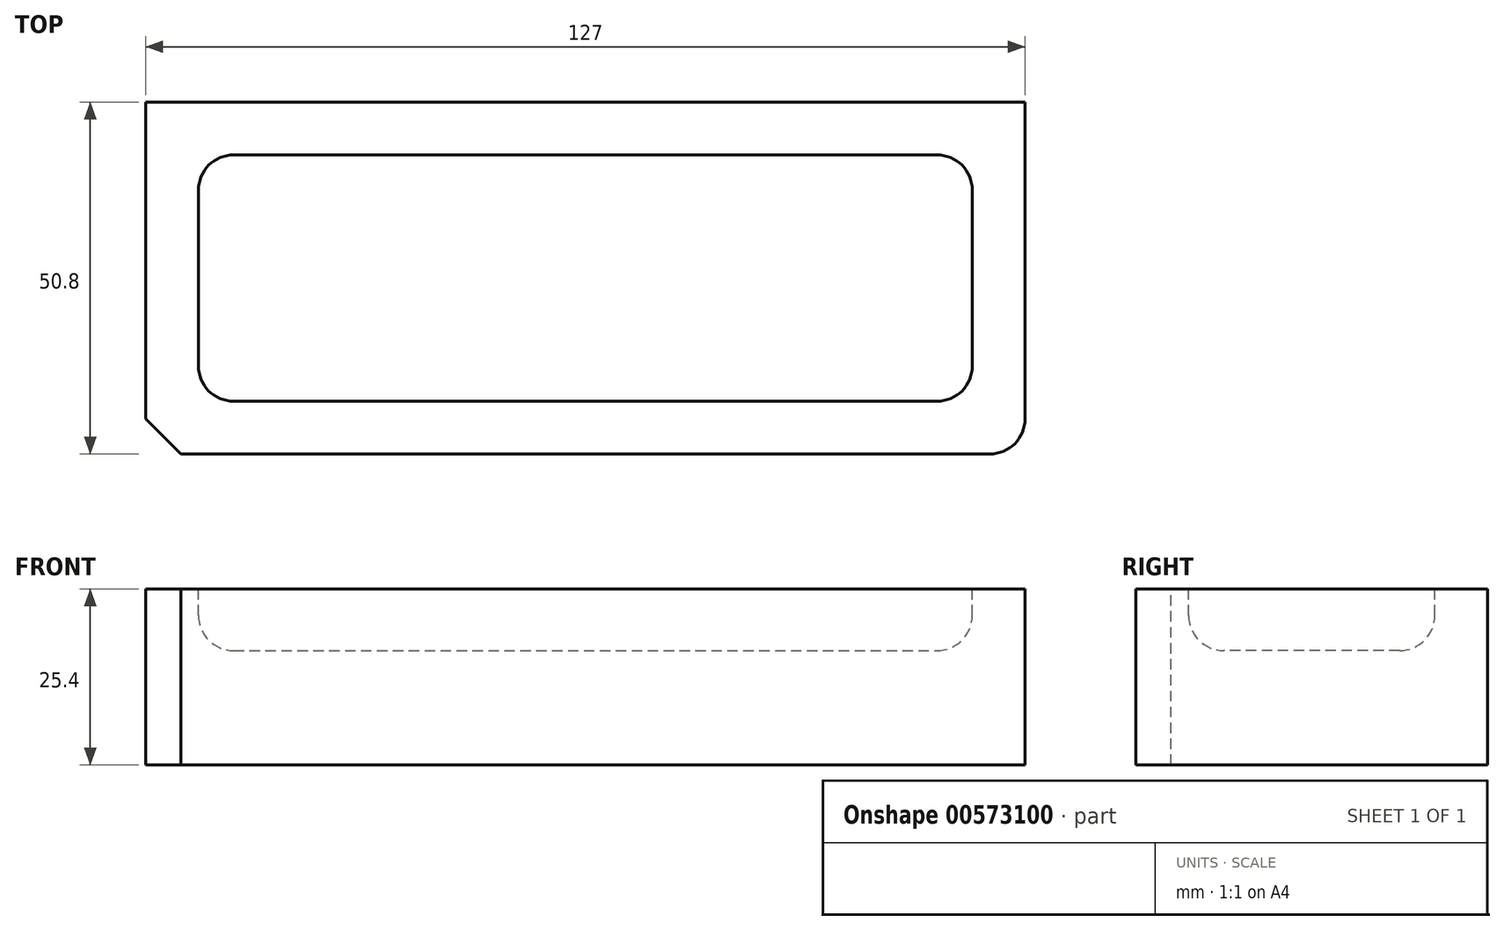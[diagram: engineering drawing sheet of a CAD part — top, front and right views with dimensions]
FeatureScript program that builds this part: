
annotation { "Feature Type Name" : "Feature", "Feature Type Description" : "" }
export const myFeature = defineFeature(function(context is Context, id is Id, definition is map)
    precondition{}
    {
        {
            var Q0;
            Q0=qCreatedBy(makeId("Top.planeOp"),FACE);
            var sketch = newSketch(context, id + "F0", { "sketchPlane" : qUnion([Q0])});
            skLineSegment(sketch, "E0.bottom", {"start": v(-63.5, 25.4) * mm, "end": v(63.5, 25.4) * mm});
            skLineSegment(sketch, "E0.top", {"start": v(-63.5, -25.4) * mm, "end": v(63.5, -25.4) * mm});
            skLineSegment(sketch, "E0.left", {"start": v(-63.5, 25.4) * mm, "end": v(-63.5, -25.4) * mm});
            skLineSegment(sketch, "E0.right", {"start": v(63.5, 25.4) * mm, "end": v(63.5, -25.4) * mm});
            skPoint(sketch, "E0.middle", {"position": v(0, 0) * mm});
            skSolve(sketch);
        }
        {
            var Q0;
            Q0=makeQuery(id+"F0.imprint","IMPRINT",FACE,{"disambiguationData":[TD([[makeQuery(id+"F0.imprint","IMPRINT",EDGE,{"derivedFrom":sQuery(id+"F0.wireOp",EDGE,"E0.bottom")}),-1.0]])]});
            extrude(context, id + "F1", {"entities" : qUnion([Q0]), "depth" : 25.4 * mm, "offsetDistance" : 25.4 * mm});
        }
        {
            var Q0;
            Q0=makeQuery(id+"F1.opExtrude","SWEPT_EDGE",EDGE,{"disambiguationData":[OSD([sQuery(id+"F0.wireOp",EDGE,"E0.top"),sQuery(id+"F0.wireOp",EDGE,"E0.left")])]});
            chamfer(context, id + "F2", {"entities" : qUnion([Q0]), "width" : 5.08 * mm, "tangentPropagation" : true});
        }
        {
            var Q0;
            Q0=makeQuery(id+"F1.opExtrude","SWEPT_EDGE",EDGE,{"disambiguationData":[OSD([sQuery(id+"F0.wireOp",EDGE,"E0.top"),sQuery(id+"F0.wireOp",EDGE,"E0.right")])]});
            fillet(context, id + "F3", {"entities" : qUnion([Q0]), "radius" : 5.08 * mm, "tangentPropagation" : true, "allowEdgeOverflow" : false});
        }
        {
            var Q0;
            Q0=makeQuery(id+"F1.opExtrude","CAP_FACE",FACE,{"disambiguationData":[OSD([sQuery(id+"F0.wireOp",EDGE,"E0.bottom"),sQuery(id+"F0.wireOp",EDGE,"E0.top"),sQuery(id+"F0.wireOp",EDGE,"E0.left"),sQuery(id+"F0.wireOp",EDGE,"E0.right")])],"isStart":false});
            var sketch = newSketch(context, id + "F4", { "sketchPlane" : qUnion([Q0])});
            skLineSegment(sketch, "E1.0", {"start": v(-55.88, 17.78) * mm, "end": v(-55.88, -17.78) * mm});
            skLineSegment(sketch, "E1.1", {"start": v(-55.88, 17.78) * mm, "end": v(55.88, 17.78) * mm});
            skLineSegment(sketch, "E1.2", {"start": v(55.88, 17.78) * mm, "end": v(55.88, -17.78) * mm});
            skLineSegment(sketch, "E1.3", {"start": v(-55.88, -17.78) * mm, "end": v(55.88, -17.78) * mm});
            skSolve(sketch);
        }
        {
            var Q0;
            Q0=makeQuery(id+"F4.imprint","IMPRINT",FACE,{"disambiguationData":[TD([[makeQuery(id+"F4.imprint","IMPRINT",EDGE,{"derivedFrom":sQuery(id+"F4.wireOp",EDGE,"E1.0")}),1.0]])]});
            extrude(context, id + "F5", {"entities" : qUnion([Q0]), "operationType" : NewBodyOperationType.REMOVE, "oppositeDirection" : true, "depth" : 8.9 * mm, "offsetDistance" : 25.4 * mm});
        }
        {
            var Q0;
            Q0=makeQuery(id+"F5.boolean.opBoolean","COPY",FACE,{"derivedFrom":makeQuery(id+"F5.opExtrude","CAP_FACE",FACE,{"disambiguationData":[OSD([sQuery(id+"F4.wireOp",EDGE,"E1.0"),sQuery(id+"F4.wireOp",EDGE,"E1.1"),sQuery(id+"F4.wireOp",EDGE,"E1.2"),sQuery(id+"F4.wireOp",EDGE,"E1.3")])],"isStart":false})});
            var Q1;
            Q1=makeQuery(id+"F5.boolean.opBoolean","COPY",EDGE,{"derivedFrom":makeQuery(id+"F5.opExtrude","SWEPT_EDGE",EDGE,{"disambiguationData":[OSD([sQuery(id+"F4.wireOp",EDGE,"E1.0"),sQuery(id+"F4.wireOp",EDGE,"E1.1")])]})});
            var Q2;
            Q2=makeQuery(id+"F5.boolean.opBoolean","COPY",EDGE,{"derivedFrom":makeQuery(id+"F5.opExtrude","SWEPT_EDGE",EDGE,{"disambiguationData":[OSD([sQuery(id+"F4.wireOp",EDGE,"E1.0"),sQuery(id+"F4.wireOp",EDGE,"E1.3")])]})});
            var Q3;
            Q3=makeQuery(id+"F5.boolean.opBoolean","COPY",EDGE,{"derivedFrom":makeQuery(id+"F5.opExtrude","SWEPT_EDGE",EDGE,{"disambiguationData":[OSD([sQuery(id+"F4.wireOp",EDGE,"E1.2"),sQuery(id+"F4.wireOp",EDGE,"E1.3")])]})});
            var Q4;
            Q4=makeQuery(id+"F5.boolean.opBoolean","COPY",EDGE,{"derivedFrom":makeQuery(id+"F5.opExtrude","SWEPT_EDGE",EDGE,{"disambiguationData":[OSD([sQuery(id+"F4.wireOp",EDGE,"E1.1"),sQuery(id+"F4.wireOp",EDGE,"E1.2")])]})});
            fillet(context, id + "F6", {"entities" : qUnion([Q0, Q1, Q2, Q3, Q4]), "radius" : 5.08 * mm, "tangentPropagation" : true, "allowEdgeOverflow" : false});
        }
    });
